# Revit family: 1570 -SAR
name_source: partatom
category: Lighting Fixtures
revit_build: Autodesk Revit 2018 (Build: 20180423_1000(x64)
units: mm (PartAtom-declared; Revit-internal decimal feet)

## family parameters
Always vertical = Yes
Cut with Voids When Loaded = No
Host = Wall
Light Source = Yes
OmniClass Number = 23.80.70.00
OmniClass Title = Lighting
Part Type = Normal
Room Calculation Point = No
Round Connector Dimension = Use Diameter
Shared = No

## types (1)
- On 6" Wall
    Apparent Load = 110 VA
    Color Filter = 16777215
    Deflector Face = 0' - 1 5/32"
    Deflector Height = 0' - 3 1/2"
    Dimming Lamp Color Temperature Shift = <None>
    Emit Shape Visible in Rendering = Yes
    Emit from Rectangle Length = 0' - 4"
    Emit from Rectangle Width = 0' - 0 3/4"
    Height = 6' - 3 31/32"
    Manufacturer = Brownlee Lighting
    Model = 1575
    Photometric Web File = 1570-B12LED-35K_Orient_Fix.ies
    Tilt Angle = 90.00°
    Type Comments = C24 - 35K
    Wattage Comments = 12
    offset to wall face = 0' - 0"

## geometry (parser evidence)
native form markers: Sweep x4
no freeform markers — native parametric forms only
